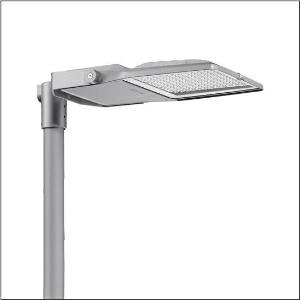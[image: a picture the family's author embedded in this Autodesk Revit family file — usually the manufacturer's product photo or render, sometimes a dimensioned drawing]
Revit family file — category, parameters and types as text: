
# Revit family: floodlight_fl_21_iq_midi___pl33t_5xa7782f2f3a_348f
name_source: partatom
category: Lighting Fixtures
units: mm (PartAtom-declared; Revit-internal decimal feet)

## family parameters
Cut with Voids When Loaded = No
Host = Face
Light Source = No
Part Type = Normal
Room Calculation Point = No
Round Connector Dimension = Use Diameter
Shared = No

## types (1)
- --- (1 x LED, 35350 lm, 270.2 W, 3000K)
    Apparent Load = 270 VA
    CIE Flux Codes = 26 75 99 100 100
    Color Rendering = 70
    Color Temperature = 3000K
    Default Elevation = 1800 mm
    Description = Floodlight FL 21 iQ midi, floodlight, primary light control with lens, of PMMA, primary optical cover: protective disc, of toughened safety glass, transparent, light distribution: PL33T, light emission: direct distribution, installation type: surface-mounted, lamps: LED, High Power LED, rated values: 35.350lm | 270,2W | 130,8lm/W (begin service life); end service life: 35.350lm | 286,6W; at 50% lumin. flux: 17.675lm | 117,4W | 150,6lm/W, colour temperature: 3000K, colour rendering: CRI > 70, light colour: 730, light setting 1 begin service life: 100% | 35.350lm | 270,2W | 130,8lm/W | 3.000K, light setting 1 end service life: 286,6W, further light settings possible, control: optimised constant luminous flux control (CLO 2.0), Desk-Remote (wireless, voltage-free reading and setting of iQ features in the workshop via application-optimized NFC function/RFID function), Smart-Wire, Night-Set, Temp-Guard, Auto-Match, Street-Remote, pre-setting: linear dimming characteristic, with terminal, 6-pole, mains connection: 220..240V, AC, 50/60Hz, luminaire housing, of diecast aluminium, powder-coated, SITECO metallic grey (DB 702S), corrosivity category C5 mid according to DIN EN ISO 12944suitable for swimming poolschlorine-resistant, sealing non-destructively replaceable, please order mast flange separately, mast bracket, of steel, galvanised, powder-coated, SITECO metallic grey (DB 702S), protection rating (complete): IP66, insulation class (complete): insulation class II (safety insulation), certification: CE, ENEC, VDE, protection symbol: D, impact resistance: IK08, permissible operating ambient temperature: -40..+40°C, permissible operating ambient temperature for outdoor applications: -40..+50°C, standard: DIN EN 12944, LABS conformity tested according to VDMA 24364:2018-05, packaging unit: 1 piece

Light Distribution: PL33T
    Height = 76 mm
    Lamp = 1 x LED
    Lamp Light Flux = 35350 lm
    Lamp Power = 270.2 W
    Lamp count = 1
    Length = 657 mm
    Luminous efficacy = 131 lm/W
    Manufacturer = Siteco
    ModVariant = No
    Model = 5XA7782F2F3A
    Mounting Place = Pole
    Mounting Type = Pole annexe
    Number of Poles = 1
    OnlyDefault = Yes
    Power Factor = 1
    Product Name = Floodlight FL 21 iQ midi | PL33T
    Product group = floodlight | pylon annexe
    ProductGroupID = 6201
    Protection Class = Protection class II
    Protection Degree = IP 66
    RLX_Detail_Level = 1
    RLX_Emergency_Light_Flux = 0 lm
    RLX_Emergency_Type = 0
    RLX_Emergency_Type_DB = No
    RlxData = <blob elided: 153821 chars, md5=fd4d4a7c>
    Socket = socket
    Standby Power = 0 W
    System Light Flux = 35350 lm
    System Power = 270 W
    Type Comments = factory setting: luminous flux: 100 % | dim-lin: 254 | 620 mA
    Type Image = l_1007123.jpg
    URL = http://relux.com
    VarID = @adj_104875
    Voltage = 0 V
    Weight = 0.00 kg
    Width = 442 mm

## geometry (parser evidence)
native form markers: Blend x4, Sweep x15
no freeform markers — native parametric forms only
